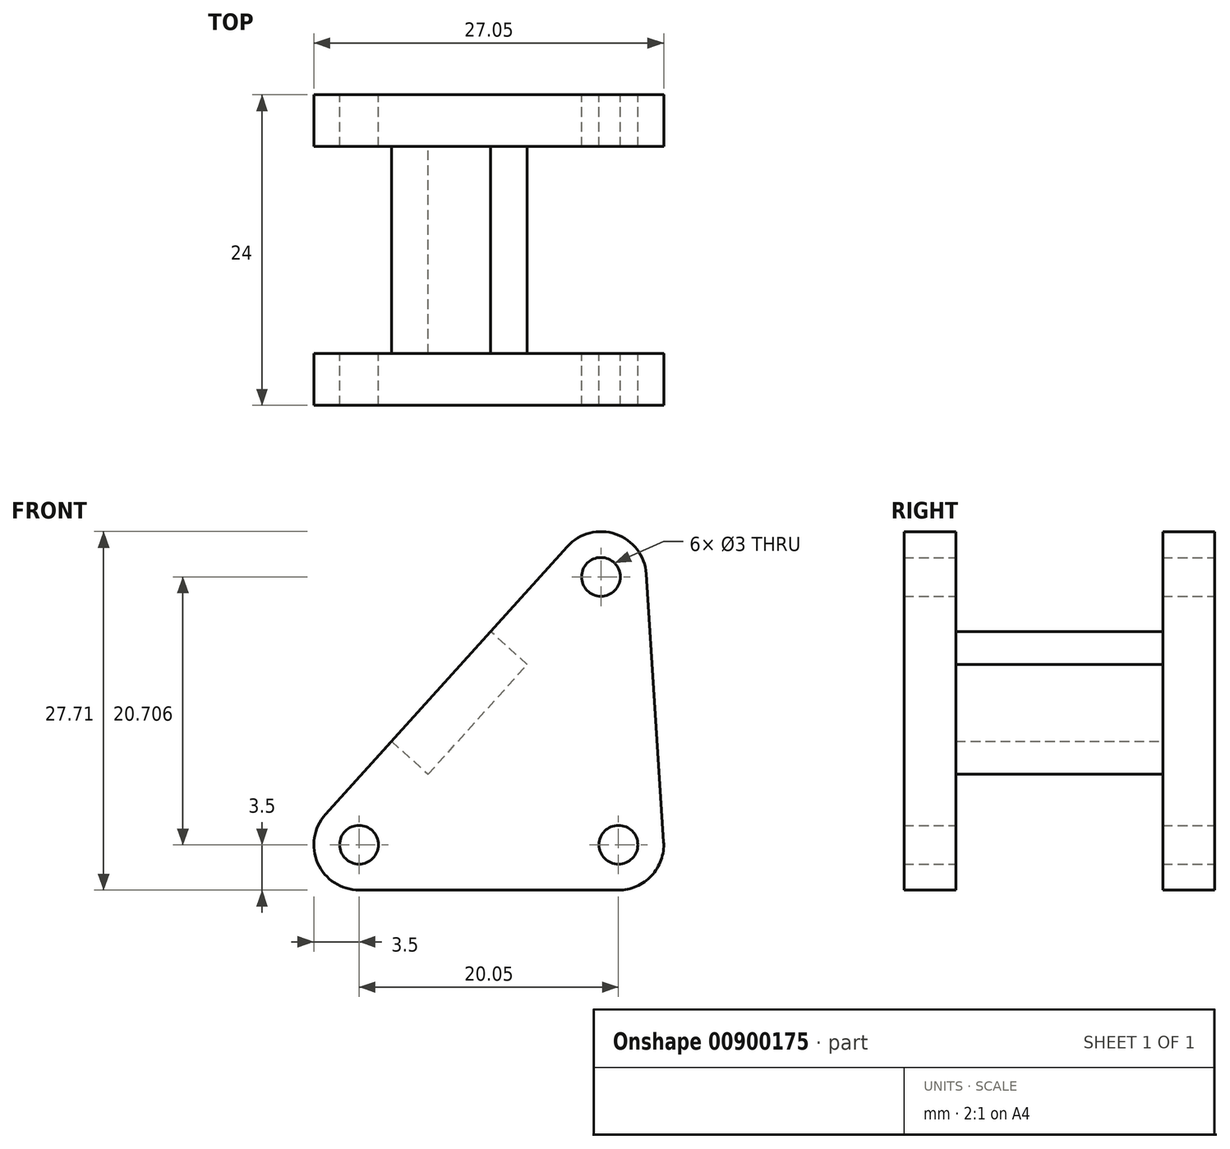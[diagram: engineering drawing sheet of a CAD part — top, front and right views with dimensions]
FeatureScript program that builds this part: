
annotation { "Feature Type Name" : "Feature", "Feature Type Description" : "" }
export const myFeature = defineFeature(function(context is Context, id is Id, definition is map)
    precondition{}
    {
        {
            var Q0;
            Q0=qCreatedBy(makeId("Front.planeOp"),FACE);
            var sketch = newSketch(context, id + "F0", { "sketchPlane" : qUnion([Q0])});
            skCircle(sketch, "E0", {"center": v(0, 0) * mm, "radius": 1.5 * mm});
            skCircle(sketch, "E1", {"center": v(20.05, 0) * mm, "radius": 1.5 * mm});
            skCircle(sketch, "E2", {"center": v(18.7, 20.7) * mm, "radius": 1.5 * mm});
            skLineSegment(sketch, "E3", {"start": v(-2.6, 2.35) * mm, "end": v(16.1, 23.05) * mm});
            skLineSegment(sketch, "E4", {"start": v(22.2, 20.93) * mm, "end": v(23.54, 0.23) * mm});
            skLineSegment(sketch, "E5", {"start": v(20.05, -3.5) * mm, "end": v(0, -3.5) * mm});
            skPoint(sketch, "E6.visualSharp", {"position": v(-7.88, -3.5) * mm});
            skArc(sketch, "E6.filletArc", {"start": v(-2.6, 2.35) * mm, "mid": v(-3.2, -1.42) * mm, "end": v(0, -3.5) * mm});
            skPoint(sketch, "E7.visualSharp", {"position": v(23.79, -3.5) * mm});
            skArc(sketch, "E7.filletArc", {"start": v(20.05, -3.5) * mm, "mid": v(22.6, -2.4) * mm, "end": v(23.54, 0.23) * mm});
            skPoint(sketch, "E8.visualSharp", {"position": v(21.65, 29.2) * mm});
            skArc(sketch, "E8.filletArc", {"start": v(22.2, 20.93) * mm, "mid": v(19.85, 24.01) * mm, "end": v(16.1, 23.05) * mm});
            skSolve(sketch);
        }
        {
            var Q0;
            Q0 = qSketchRegion(id + "F0", true);
            extrude(context, id + "F1", {"entities" : qUnion([Q0]), "endBound" : BoundingType.SYMMETRIC, "depth" : 24 * mm, "offsetDistance" : 25.4 * mm});
        }
        {
            var Q0;
            Q0=qCreatedBy(makeId("Front.planeOp"),FACE);
            var sketch = newSketch(context, id + "F2", { "sketchPlane" : qUnion([Q0])});
            skLineSegment(sketch, "E9", {"start": v(2.5, 8) * mm, "end": v(5.34, 5.45) * mm});
            skLineSegment(sketch, "E10", {"start": v(5.34, 5.45) * mm, "end": v(13, 13.93) * mm});
            skLineSegment(sketch, "E11", {"start": v(13, 13.93) * mm, "end": v(10.17, 16.48) * mm});
            skLineSegment(sketch, "E12", {"start": v(10.17, 16.48) * mm, "end": v(2.5, 8) * mm});
            skSolve(sketch);
        }
        {
            var Q0;
            Q0=qCreatedBy(makeId("Front.planeOp"),FACE);
            var sketch = newSketch(context, id + "F3", { "sketchPlane" : qUnion([Q0])});
            skLineSegment(sketch, "E13.0.0", {"start": v(0, -3.5) * mm, "end": v(20.05, -3.5) * mm});
            skArc(sketch, "E13.0.1", {"start": v(20.05, -3.5) * mm, "mid": v(22.6, -2.4) * mm, "end": v(23.54, 0.23) * mm});
            skLineSegment(sketch, "E13.0.2", {"start": v(23.54, 0.23) * mm, "end": v(22.2, 20.93) * mm});
            skArc(sketch, "E13.0.3", {"start": v(22.2, 20.93) * mm, "mid": v(19.85, 24.01) * mm, "end": v(16.1, 23.05) * mm});
            skLineSegment(sketch, "E13.0.4", {"start": v(16.1, 23.05) * mm, "end": v(-2.6, 2.35) * mm});
            skArc(sketch, "E13.0.5", {"start": v(-2.6, 2.35) * mm, "mid": v(-3.2, -1.42) * mm, "end": v(0, -3.5) * mm});
            skSolve(sketch);
        }
        {
            var Q0;
            Q0 = qSketchRegion(id + "F3", true);
            extrude(context, id + "F4", {"entities" : qUnion([Q0]), "operationType" : NewBodyOperationType.REMOVE, "endBound" : BoundingType.SYMMETRIC, "oppositeDirection" : true, "depth" : 16 * mm, "offsetDistance" : 25.4 * mm});
        }
        {
            var Q0;
            Q0=makeQuery(id+"F2.imprint","IMPRINT",FACE,{"disambiguationData":[TD([[makeQuery(id+"F2.imprint","IMPRINT",EDGE,{"derivedFrom":sQuery(id+"F2.wireOp",EDGE,"E9")}),1.0]])]});
            extrude(context, id + "F5", {"entities" : qUnion([Q0]), "endBound" : BoundingType.SYMMETRIC, "depth" : 16 * mm, "offsetDistance" : 25.4 * mm});
        }
    });
